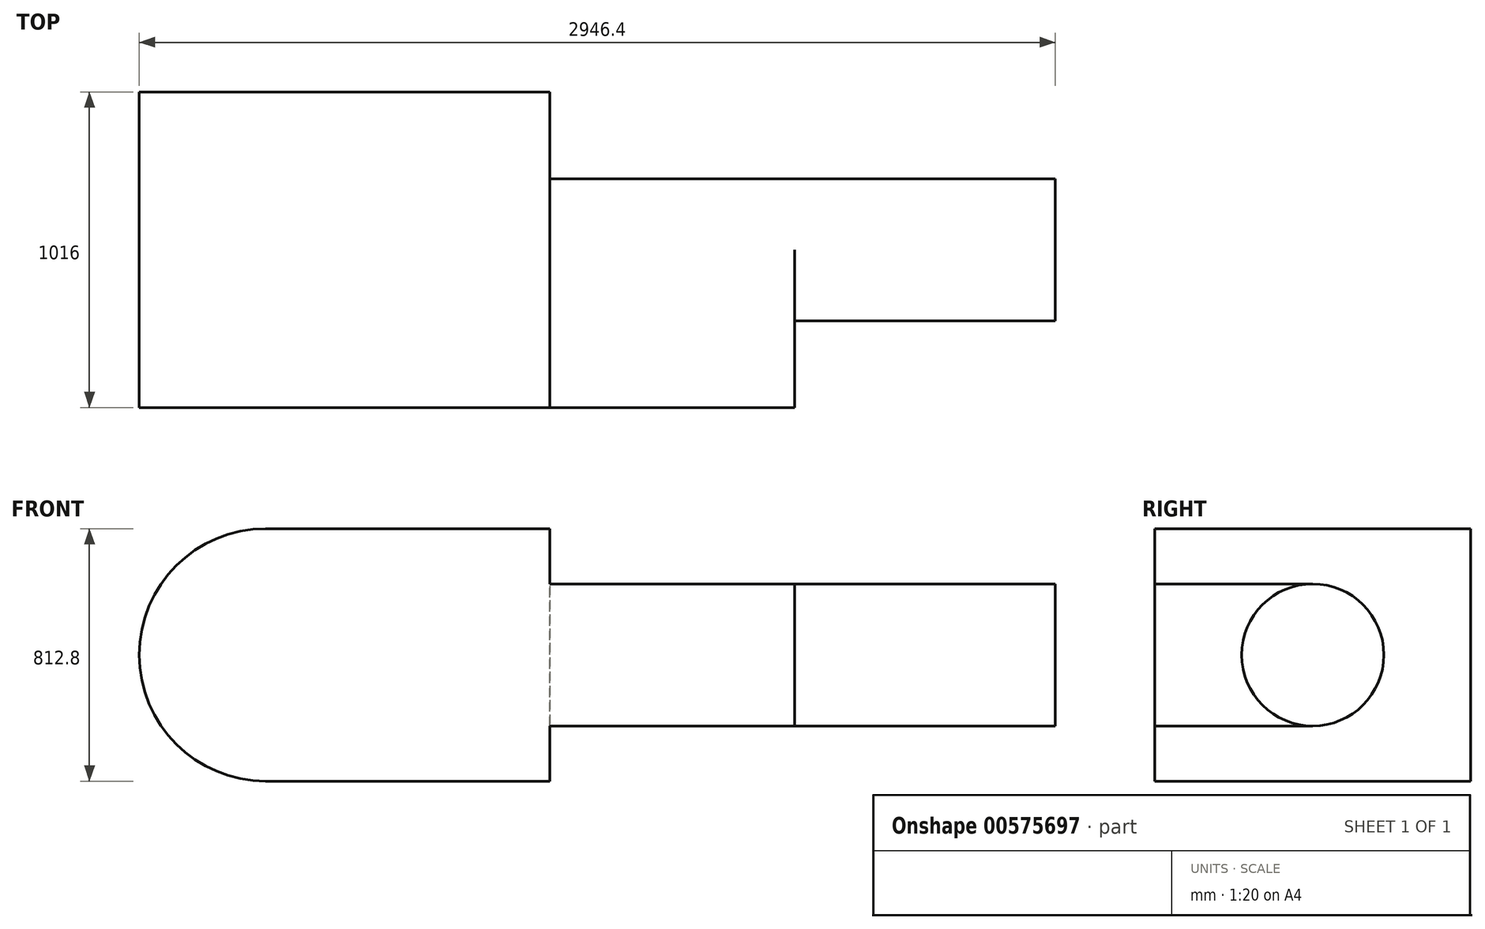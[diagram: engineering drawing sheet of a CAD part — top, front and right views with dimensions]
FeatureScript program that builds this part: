
annotation { "Feature Type Name" : "Feature", "Feature Type Description" : "" }
export const myFeature = defineFeature(function(context is Context, id is Id, definition is map)
    precondition{}
    {
        {
            var Q0;
            Q0=qCreatedBy(makeId("Front.planeOp"),FACE);
            var sketch = newSketch(context, id + "F0", { "sketchPlane" : qUnion([Q0])});
            skCircle(sketch, "E0", {"center": v(0, 0) * mm, "radius": 406.4 * mm});
            skLineSegment(sketch, "E1.bottom", {"start": v(0, 406.4) * mm, "end": v(914.4, 406.4) * mm});
            skLineSegment(sketch, "E1.top", {"start": v(0, -406.4) * mm, "end": v(914.4, -406.4) * mm});
            skLineSegment(sketch, "E1.left", {"start": v(0, 406.4) * mm, "end": v(0, -406.4) * mm});
            skLineSegment(sketch, "E1.right", {"start": v(914.4, 406.4) * mm, "end": v(914.4, -406.4) * mm});
            skLineSegment(sketch, "E2", {"start": v(914.4, 406.4) * mm, "end": v(914.4, 228.6) * mm});
            skLineSegment(sketch, "E3.bottom", {"start": v(914.4, 228.6) * mm, "end": v(1727.2, 228.6) * mm});
            skLineSegment(sketch, "E3.top", {"start": v(914.4, -228.6) * mm, "end": v(1727.2, -228.6) * mm});
            skLineSegment(sketch, "E3.left", {"start": v(914.4, 228.6) * mm, "end": v(914.4, -228.6) * mm});
            skLineSegment(sketch, "E3.right", {"start": v(1727.2, 228.6) * mm, "end": v(1727.2, -228.6) * mm});
            skSolve(sketch);
        }
        {
            var Q0;
            Q0 = qSketchRegion(id + "F0", true);
            extrude(context, id + "F1", {"entities" : qUnion([Q0]), "depth" : 1016 * mm, "offsetDistance" : 25.4 * mm});
        }
        {
            var Q0;
            Q0=makeQuery(id+"F1.opExtrude","SWEPT_FACE",FACE,{"disambiguationData":[OSD([sQuery(id+"F0.wireOp",EDGE,"E3.right")])]});
            var sketch = newSketch(context, id + "F2", { "sketchPlane" : qUnion([Q0])});
            skCircle(sketch, "E4", {"center": v(-508, 0) * mm, "radius": 228.6 * mm});
            skSolve(sketch);
        }
        {
            var Q0;
            {var subQ0=sQuery(id+"F2.wireOp",EDGE,"ftTgj08B-vHkr-LiIJ-Fw9q-Y5DC9cSDudk1");Q0=makeQuery(id+"F2.imprint","IMPRINT",FACE,{"disambiguationData":[TD([[makeQuery(id+"F2.imprint","IMPRINT",EDGE,{"derivedFrom":subQ0}),-1.0]])]});}
            var Q1;
            {var subQ1=sQuery(id+"F0.wireOp",EDGE,"E3.right");var subQ6=makeQuery(id+"F1.opExtrude","CAP_EDGE",EDGE,{"disambiguationData":[OSD([subQ1])],"isStart":true});Q1=makeQuery(id+"F2.imprint","IMPRINT",FACE,{"disambiguationData":[TD([[makeQuery(id+"F2.imprint","IMPRINT",EDGE,{"derivedFrom":subQ6}),-1.0]])]});}
            extrude(context, id + "F3", {"entities" : qUnion([Q0, Q1]), "operationType" : NewBodyOperationType.REMOVE, "oppositeDirection" : true, "depth" : 812.8 * mm, "offsetDistance" : 25.4 * mm});
        }
        {
            var Q0;
            {var subQ0=sQuery(id+"F2.wireOp",EDGE,"E4");var subQ1=sQuery(id+"F0.wireOp",EDGE,"E3.right");var subQ2=makeQuery(id+"F2.imprint","INTERSECT",VERTEX,{"derivedFrom":[makeQuery(id+"F1.opExtrude","SWEPT_EDGE",EDGE,{"disambiguationData":[OSD([sQuery(id+"F0.wireOp",EDGE,"E3.bottom"),subQ1])]}),subQ0]});Q0=makeQuery(id+"F2.imprint","IMPRINT",FACE,{"disambiguationData":[TD([[makeQuery(id+"F2.imprint","IMPRINT",EDGE,{"disambiguationData":[TD([[subQ2,-1.0]])],"derivedFrom":subQ0}),1.0]])]});}
            extrude(context, id + "F4", {"entities" : qUnion([Q0]), "operationType" : NewBodyOperationType.ADD, "depth" : 812.8 * mm, "offsetDistance" : 25.4 * mm});
        }
        {
            var Q0;
            {var subQ1=sQuery(id+"F0.wireOp",EDGE,"E3.right");var subQ6=makeQuery(id+"F1.opExtrude","CAP_EDGE",EDGE,{"disambiguationData":[OSD([subQ1])],"isStart":false});Q0=makeQuery(id+"F2.imprint","IMPRINT",FACE,{"disambiguationData":[TD([[makeQuery(id+"F2.imprint","IMPRINT",EDGE,{"derivedFrom":subQ6}),1.0]])]});}
            extrude(context, id + "F5", {"entities" : qUnion([Q0]), "operationType" : NewBodyOperationType.REMOVE, "oppositeDirection" : true, "depth" : 25.4 * mm, "offsetDistance" : 25.4 * mm});
        }
    });
